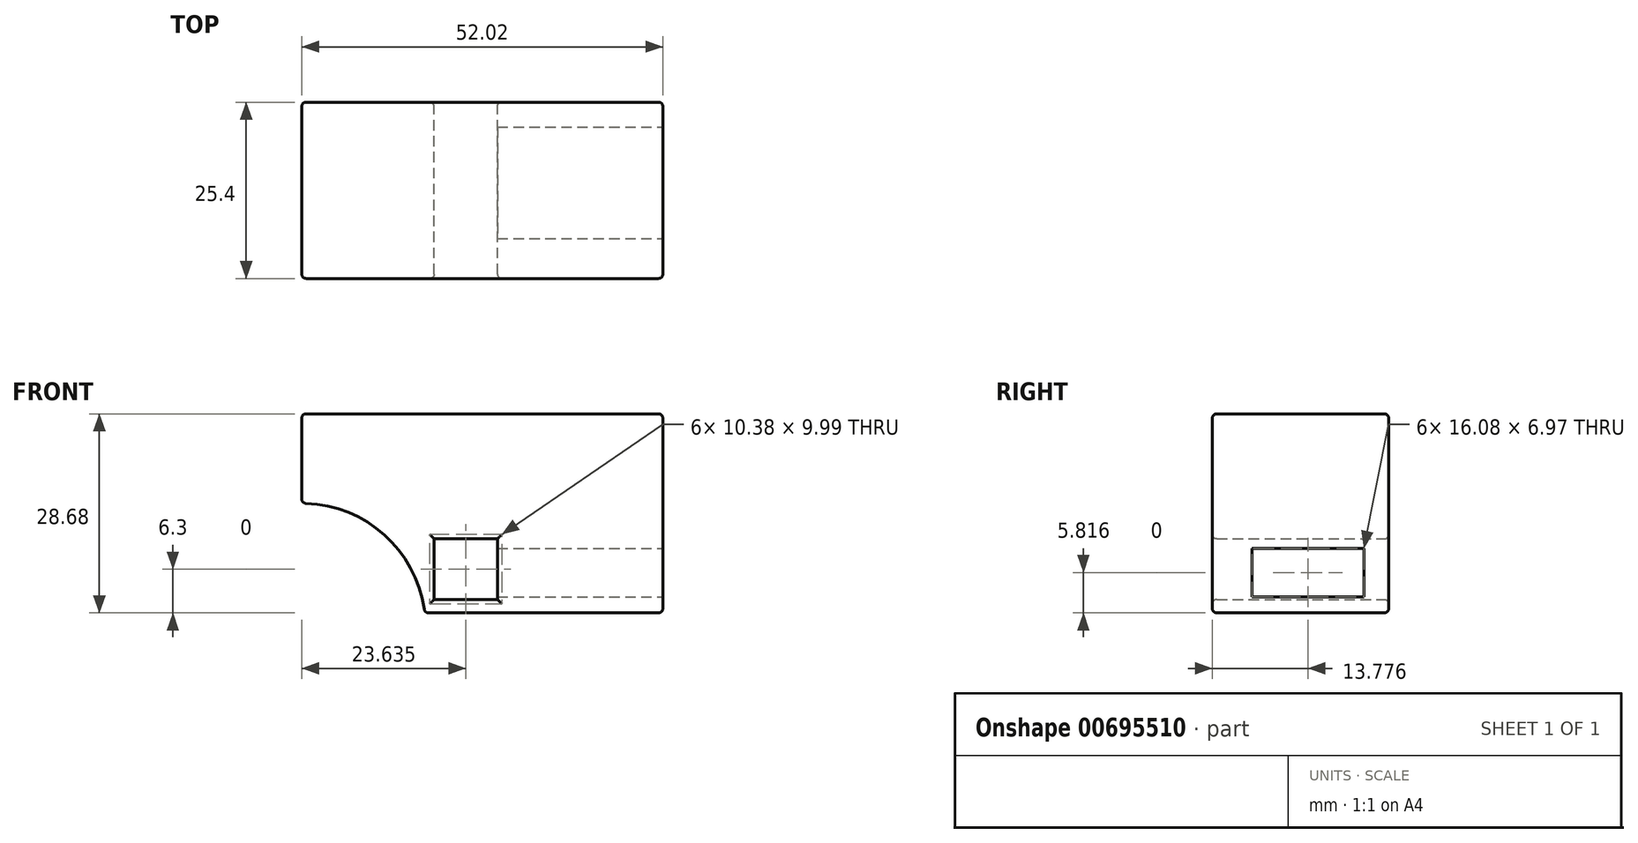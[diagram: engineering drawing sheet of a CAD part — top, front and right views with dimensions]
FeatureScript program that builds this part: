
annotation { "Feature Type Name" : "Feature", "Feature Type Description" : "" }
export const myFeature = defineFeature(function(context is Context, id is Id, definition is map)
    precondition{}
    {
        {
            var Q0;
            Q0=qCreatedBy(makeId("Front.planeOp"),FACE);
            var sketch = newSketch(context, id + "F0", { "sketchPlane" : qUnion([Q0])});
            skLineSegment(sketch, "E0.bottom", {"start": v(0, 2.03) * mm, "end": v(52.02, 2.03) * mm});
            skLineSegment(sketch, "E0.top", {"start": v(0, 30.7) * mm, "end": v(52.02, 30.7) * mm});
            skLineSegment(sketch, "E0.left", {"start": v(0, 2.03) * mm, "end": v(0, 30.7) * mm});
            skLineSegment(sketch, "E0.right", {"start": v(52.02, 2.03) * mm, "end": v(52.02, 30.7) * mm});
            skLineSegment(sketch, "E1.bottom", {"start": v(28.19, 12.69) * mm, "end": v(19.08, 12.69) * mm});
            skLineSegment(sketch, "E1.top", {"start": v(28.19, 3.97) * mm, "end": v(19.08, 3.97) * mm});
            skLineSegment(sketch, "E1.left", {"start": v(28.19, 12.69) * mm, "end": v(28.19, 3.97) * mm});
            skLineSegment(sketch, "E1.right", {"start": v(19.08, 12.69) * mm, "end": v(19.08, 3.97) * mm});
            skCircle(sketch, "E2", {"center": v(0, 0) * mm, "radius": 17.82 * mm});
            skSolve(sketch);
        }
        {
            var Q0;
            {var subQ2=sQuery(id+"F0.wireOp",EDGE,"E0.top");Q0=makeQuery(id+"F0.imprint","IMPRINT",FACE,{"disambiguationData":[TD([[makeQuery(id+"F0.imprint","IMPRINT",EDGE,{"derivedFrom":subQ2}),-1.0]])]});}
            extrude(context, id + "F1", {"entities" : qUnion([Q0]), "depth" : 25.4 * mm, "offsetDistance" : 25.4 * mm});
        }
        {
            var Q0;
            Q0=makeQuery(id+"F1.opExtrude","SWEPT_FACE",FACE,{"disambiguationData":[OSD([sQuery(id+"F0.wireOp",EDGE,"E0.right")])]});
            var sketch = newSketch(context, id + "F2", { "sketchPlane" : qUnion([Q0])});
            skLineSegment(sketch, "E3.bottom", {"start": v(-19.66, 11.33) * mm, "end": v(-3.58, 11.33) * mm});
            skLineSegment(sketch, "E3.top", {"start": v(-19.66, 4.36) * mm, "end": v(-3.58, 4.36) * mm});
            skLineSegment(sketch, "E3.left", {"start": v(-19.66, 11.33) * mm, "end": v(-19.66, 4.36) * mm});
            skLineSegment(sketch, "E3.right", {"start": v(-3.58, 11.33) * mm, "end": v(-3.58, 4.36) * mm});
            skSolve(sketch);
        }
        {
            var Q0;
            Q0=makeQuery(id+"F2.imprint","IMPRINT",FACE,{"disambiguationData":[TD([[makeQuery(id+"F2.imprint","IMPRINT",EDGE,{"derivedFrom":sQuery(id+"F2.wireOp",EDGE,"E3.bottom")}),-1.0]])]});
            extrude(context, id + "F3", {"entities" : qUnion([Q0]), "operationType" : NewBodyOperationType.REMOVE, "endBound" : BoundingType.UP_TO_NEXT, "oppositeDirection" : true, "depth" : 50.8 * mm, "offsetDistance" : 25.4 * mm});
        }
        {
            var Q0;
            Q0=makeQuery(id+"F1.opExtrude","CAP_EDGE",EDGE,{"disambiguationData":[OSD([sQuery(id+"F0.wireOp",EDGE,"E1.top")])],"isStart":false});
            var Q1;
            Q1=makeQuery(id+"F1.opExtrude","CAP_EDGE",EDGE,{"disambiguationData":[OSD([sQuery(id+"F0.wireOp",EDGE,"E1.right")])],"isStart":false});
            var Q2;
            Q2=makeQuery(id+"F1.opExtrude","CAP_EDGE",EDGE,{"disambiguationData":[OSD([sQuery(id+"F0.wireOp",EDGE,"E1.bottom")])],"isStart":false});
            var Q3;
            Q3=makeQuery(id+"F1.opExtrude","CAP_EDGE",EDGE,{"disambiguationData":[OSD([sQuery(id+"F0.wireOp",EDGE,"E1.left")])],"isStart":false});
            var Q4;
            Q4=makeQuery(id+"F3.boolean.opBoolean","COPY",EDGE,{"derivedFrom":makeQuery(id+"F3.opExtrude","CAP_EDGE",EDGE,{"disambiguationData":[OSD([sQuery(id+"F2.wireOp",EDGE,"E3.top")])],"isStart":true})});
            var Q5;
            Q5=makeQuery(id+"F3.boolean.opBoolean","COPY",EDGE,{"derivedFrom":makeQuery(id+"F3.opExtrude","CAP_EDGE",EDGE,{"disambiguationData":[OSD([sQuery(id+"F2.wireOp",EDGE,"E3.left")])],"isStart":true})});
            var Q6;
            Q6=makeQuery(id+"F3.boolean.opBoolean","COPY",EDGE,{"derivedFrom":makeQuery(id+"F3.opExtrude","CAP_EDGE",EDGE,{"disambiguationData":[OSD([sQuery(id+"F2.wireOp",EDGE,"E3.bottom")])],"isStart":true})});
            var Q7;
            Q7=makeQuery(id+"F3.boolean.opBoolean","COPY",EDGE,{"derivedFrom":makeQuery(id+"F3.opExtrude","CAP_EDGE",EDGE,{"disambiguationData":[OSD([sQuery(id+"F2.wireOp",EDGE,"E3.right")])],"isStart":true})});
            fillet(context, id + "F4", {"entities" : qUnion([Q0, Q1, Q2, Q3, Q4, Q5, Q6, Q7]), "radius" : 0.64 * mm, "tangentPropagation" : true, "allowEdgeOverflow" : false});
        }
        {
            var Q0;
            Q0=makeQuery(id+"F3.boolean.opBoolean","COPY",EDGE,{"derivedFrom":makeQuery(id+"F3.opExtrude","CAP_EDGE",EDGE,{"disambiguationData":[OSD([sQuery(id+"F2.wireOp",EDGE,"E3.bottom")])],"isStart":false})});
            var Q1;
            Q1=makeQuery(id+"F3.boolean.opBoolean","COPY",EDGE,{"derivedFrom":makeQuery(id+"F3.opExtrude","CAP_EDGE",EDGE,{"disambiguationData":[OSD([sQuery(id+"F2.wireOp",EDGE,"E3.left")])],"isStart":false})});
            var Q2;
            Q2=makeQuery(id+"F3.boolean.opBoolean","COPY",EDGE,{"derivedFrom":makeQuery(id+"F3.opExtrude","CAP_EDGE",EDGE,{"disambiguationData":[OSD([sQuery(id+"F2.wireOp",EDGE,"E3.right")])],"isStart":false})});
            var Q3;
            Q3=makeQuery(id+"F3.boolean.opBoolean","COPY",EDGE,{"derivedFrom":makeQuery(id+"F3.opExtrude","CAP_EDGE",EDGE,{"disambiguationData":[OSD([sQuery(id+"F2.wireOp",EDGE,"E3.top")])],"isStart":false})});
            var Q4;
            Q4=makeQuery(id+"F1.opExtrude","CAP_EDGE",EDGE,{"disambiguationData":[OSD([sQuery(id+"F0.wireOp",EDGE,"E1.left")])],"isStart":true});
            var Q5;
            Q5=makeQuery(id+"F1.opExtrude","CAP_EDGE",EDGE,{"disambiguationData":[OSD([sQuery(id+"F0.wireOp",EDGE,"E1.right")])],"isStart":true});
            var Q6;
            Q6=makeQuery(id+"F1.opExtrude","CAP_EDGE",EDGE,{"disambiguationData":[OSD([sQuery(id+"F0.wireOp",EDGE,"E1.bottom")])],"isStart":true});
            var Q7;
            Q7=makeQuery(id+"F1.opExtrude","CAP_EDGE",EDGE,{"disambiguationData":[OSD([sQuery(id+"F0.wireOp",EDGE,"E1.top")])],"isStart":true});
            fillet(context, id + "F5", {"entities" : qUnion([Q0, Q1, Q2, Q3, Q4, Q5, Q6, Q7]), "radius" : 0.64 * mm, "tangentPropagation" : true, "allowEdgeOverflow" : false});
        }
        {
            var Q0;
            Q0=makeQuery(id+"F1.opExtrude","CAP_EDGE",EDGE,{"disambiguationData":[OSD([sQuery(id+"F0.wireOp",EDGE,"E2")])],"isStart":true});
            var Q1;
            Q1=makeQuery(id+"F1.opExtrude","CAP_EDGE",EDGE,{"disambiguationData":[OSD([sQuery(id+"F0.wireOp",EDGE,"E2")])],"isStart":false});
            var Q2;
            Q2=makeQuery(id+"F1.opExtrude","SWEPT_EDGE",EDGE,{"disambiguationData":[OSD([sQuery(id+"F0.wireOp",EDGE,"E0.bottom"),sQuery(id+"F0.wireOp",EDGE,"E2")])]});
            var Q3;
            Q3=makeQuery(id+"F1.opExtrude","SWEPT_EDGE",EDGE,{"disambiguationData":[OSD([sQuery(id+"F0.wireOp",EDGE,"E0.left"),sQuery(id+"F0.wireOp",EDGE,"E2")])]});
            var Q4;
            Q4=makeQuery(id+"F1.opExtrude","CAP_EDGE",EDGE,{"disambiguationData":[OSD([sQuery(id+"F0.wireOp",EDGE,"E0.left")])],"isStart":true});
            var Q5;
            Q5=makeQuery(id+"F1.opExtrude","CAP_EDGE",EDGE,{"disambiguationData":[OSD([sQuery(id+"F0.wireOp",EDGE,"E0.left")])],"isStart":false});
            var Q6;
            Q6=makeQuery(id+"F1.opExtrude","CAP_EDGE",EDGE,{"disambiguationData":[OSD([sQuery(id+"F0.wireOp",EDGE,"E0.top")])],"isStart":true});
            var Q7;
            Q7=makeQuery(id+"F1.opExtrude","CAP_EDGE",EDGE,{"disambiguationData":[OSD([sQuery(id+"F0.wireOp",EDGE,"E0.right")])],"isStart":true});
            var Q8;
            Q8=makeQuery(id+"F1.opExtrude","CAP_EDGE",EDGE,{"disambiguationData":[OSD([sQuery(id+"F0.wireOp",EDGE,"E0.bottom")])],"isStart":true});
            var Q9;
            Q9=makeQuery(id+"F1.opExtrude","SWEPT_EDGE",EDGE,{"disambiguationData":[OSD([sQuery(id+"F0.wireOp",EDGE,"E0.top"),sQuery(id+"F0.wireOp",EDGE,"E0.right")])]});
            var Q10;
            Q10=makeQuery(id+"F1.opExtrude","CAP_EDGE",EDGE,{"disambiguationData":[OSD([sQuery(id+"F0.wireOp",EDGE,"E0.right")])],"isStart":false});
            var Q11;
            Q11=makeQuery(id+"F1.opExtrude","SWEPT_EDGE",EDGE,{"disambiguationData":[OSD([sQuery(id+"F0.wireOp",EDGE,"E0.bottom"),sQuery(id+"F0.wireOp",EDGE,"E0.right")])]});
            var Q12;
            Q12=makeQuery(id+"F1.opExtrude","CAP_EDGE",EDGE,{"disambiguationData":[OSD([sQuery(id+"F0.wireOp",EDGE,"E0.top")])],"isStart":false});
            var Q13;
            Q13=makeQuery(id+"F1.opExtrude","SWEPT_EDGE",EDGE,{"disambiguationData":[OSD([sQuery(id+"F0.wireOp",EDGE,"E0.top"),sQuery(id+"F0.wireOp",EDGE,"E0.left")])]});
            var Q14;
            Q14=makeQuery(id+"F1.opExtrude","CAP_EDGE",EDGE,{"disambiguationData":[OSD([sQuery(id+"F0.wireOp",EDGE,"E0.bottom")])],"isStart":false});
            fillet(context, id + "F6", {"entities" : qUnion([Q0, Q1, Q2, Q3, Q4, Q5, Q6, Q7, Q8, Q9, Q10, Q11, Q12, Q13, Q14]), "radius" : 0.64 * mm, "tangentPropagation" : true, "allowEdgeOverflow" : false});
        }
    });
